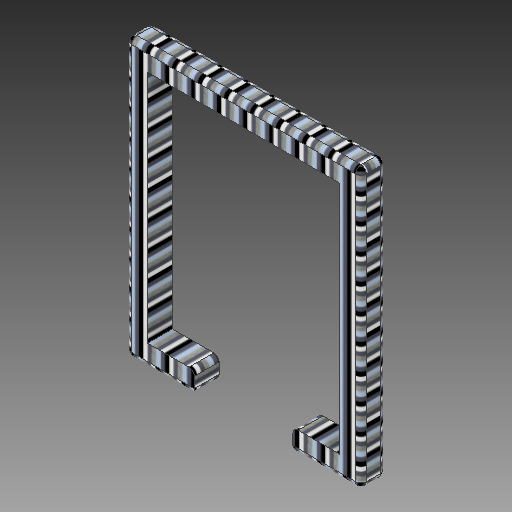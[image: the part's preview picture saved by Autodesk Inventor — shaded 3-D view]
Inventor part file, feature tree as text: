
AUTODESK INVENTOR PART (.ipt)
format: ipt  version: 2017 (Build 210142000, 142)  size: 222,208 bytes
history: native  units: in
note: dims shown in document units (in); Inventor stores cm internally (conversion verified against a paired STEP export)
features: extrude x1, fillet x1, sketch x1
ambient origin geometry x8: Origin, YZ Plane, XZ Plane, XY Plane, X Axis, Y Axis, Z Axis, Center Point
bodies: Solid1 (feature_tree)
feature tree (3):
  extrude  "Extrusion1"  Depth=33.1in
  fillet  "Fillet1"  Radius=6.6in
  sketch  "Sketch1"  dims[d0=27.1in d1=33.1in d2=6.6in d3=6.6in d4=3.0in d5=3.5in d6=0.0in d7=0.75in]
